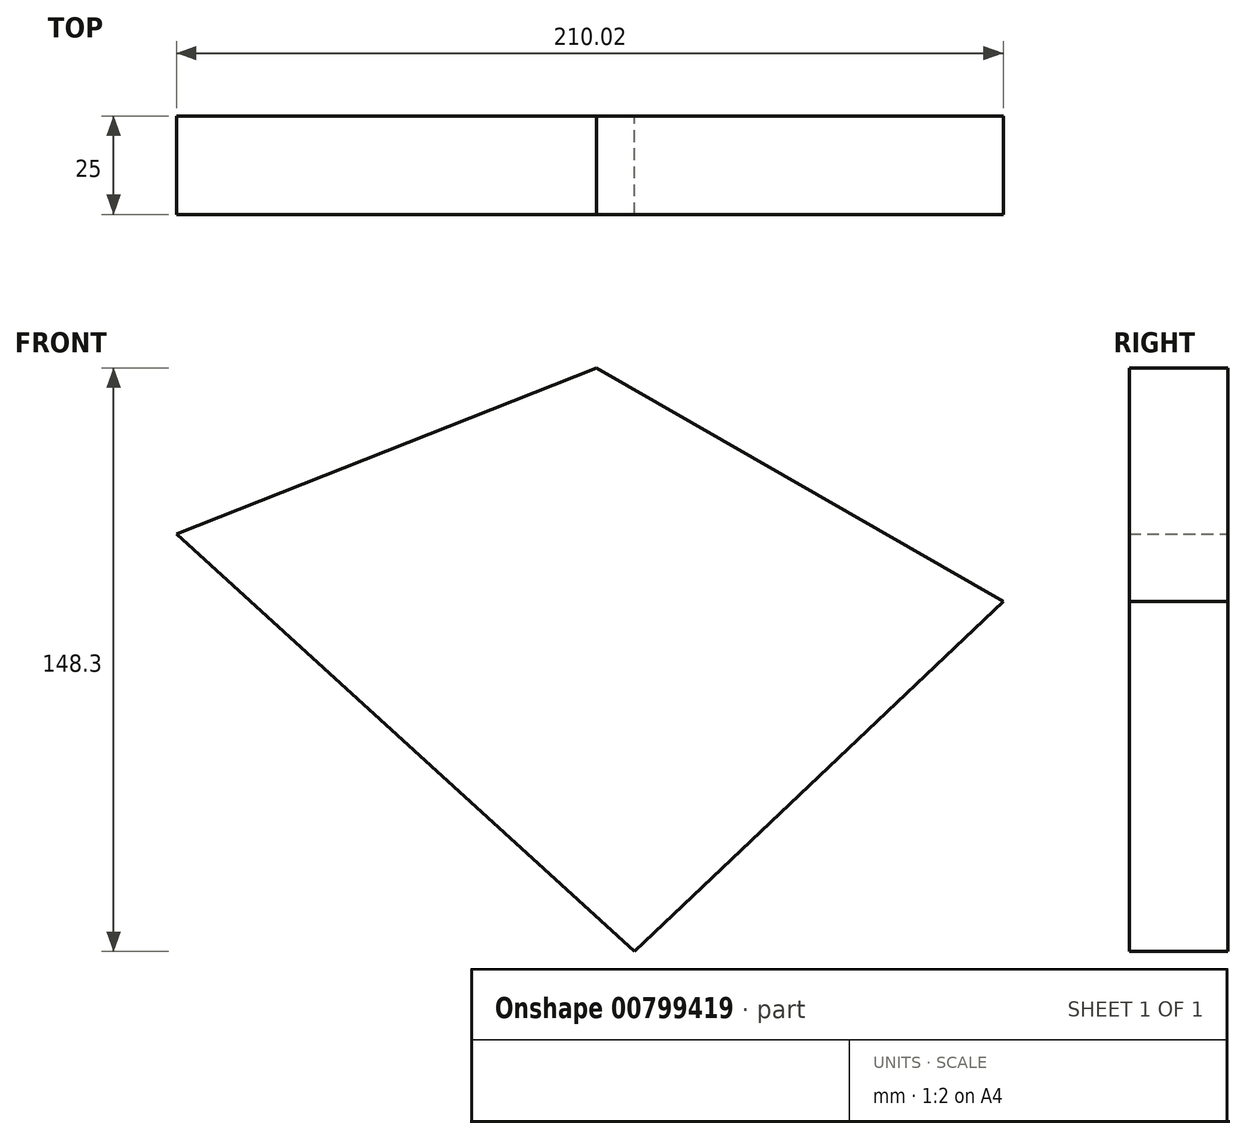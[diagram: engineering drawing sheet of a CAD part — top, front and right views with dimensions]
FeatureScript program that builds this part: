
annotation { "Feature Type Name" : "Feature", "Feature Type Description" : "" }
export const myFeature = defineFeature(function(context is Context, id is Id, definition is map)
    precondition{}
    {
        {
            var Q0;
            Q0=qCreatedBy(makeId("Front.planeOp"),FACE);
            var sketch = newSketch(context, id + "F0", { "sketchPlane" : qUnion([Q0])});
            skLineSegment(sketch, "E0", {"start": v(-106.7, 30.07) * mm, "end": v(0, 72.28) * mm});
            skLineSegment(sketch, "E1", {"start": v(0, 72.28) * mm, "end": v(103.32, 12.92) * mm});
            skLineSegment(sketch, "E2", {"start": v(103.32, 12.92) * mm, "end": v(9.64, -76.02) * mm});
            skLineSegment(sketch, "E3", {"start": v(9.64, -76.02) * mm, "end": v(-106.7, 30.07) * mm});
            skSolve(sketch);
        }
        {
            var Q0;
            Q0=makeQuery(id+"F0.imprint","IMPRINT",FACE,{"disambiguationData":[TD([[makeQuery(id+"F0.imprint","IMPRINT",EDGE,{"derivedFrom":sQuery(id+"F0.wireOp",EDGE,"E0")}),-1.0]])]});
            extrude(context, id + "F1", {"entities" : qUnion([Q0]), "depth" : 25 * mm, "offsetDistance" : 25 * mm});
        }
    });
